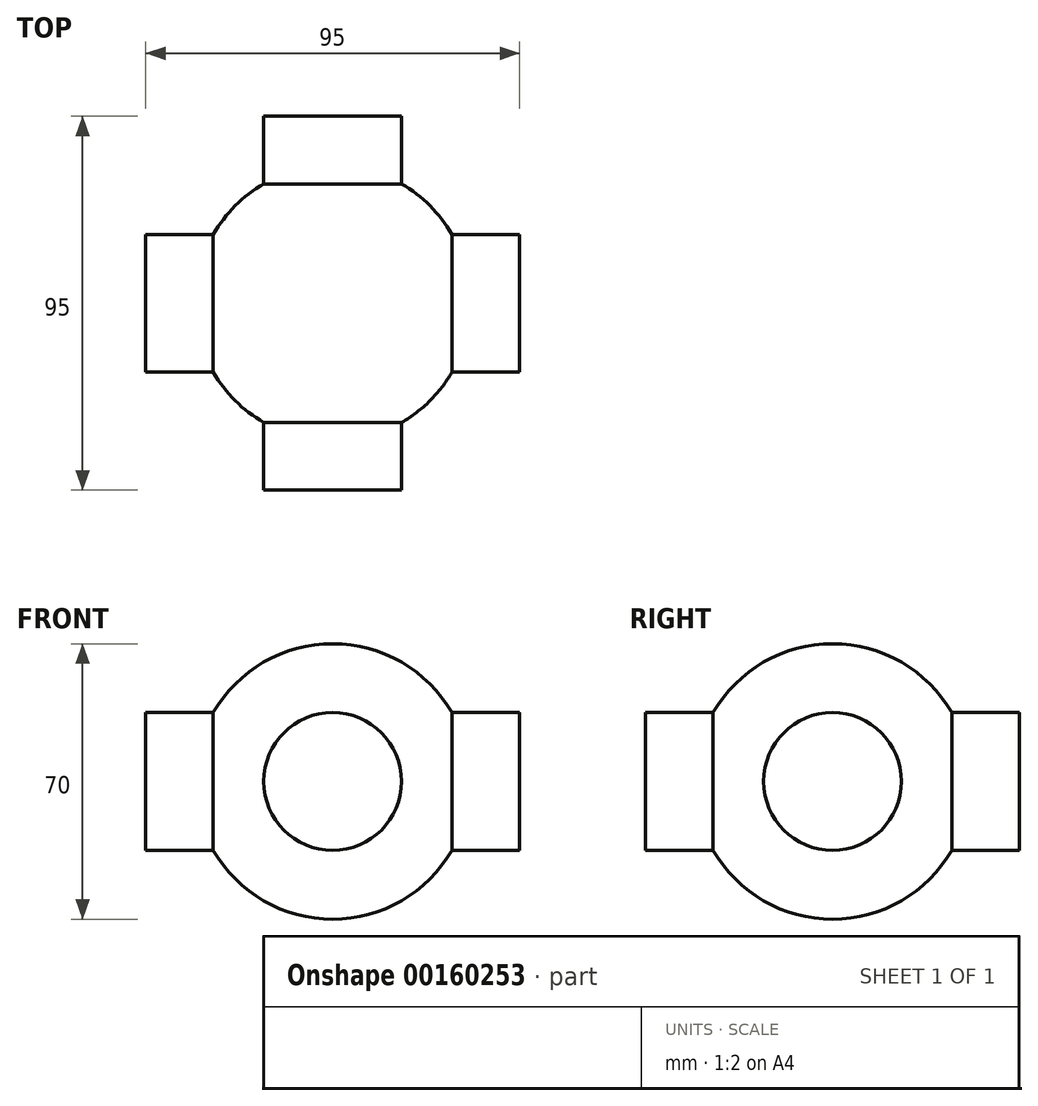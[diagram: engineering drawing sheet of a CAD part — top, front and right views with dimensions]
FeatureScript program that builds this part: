
annotation { "Feature Type Name" : "Feature", "Feature Type Description" : "" }
export const myFeature = defineFeature(function(context is Context, id is Id, definition is map)
    precondition{}
    {
        {
            var Q0;
            Q0=qCreatedBy(makeId("Front.planeOp"),FACE);
            var sketch = newSketch(context, id + "F0", { "sketchPlane" : qUnion([Q0])});
            skArc(sketch, "E0", {"start": v(0, 35) * mm, "mid": v(-35, 0) * mm, "end": v(0, -35) * mm});
            skLineSegment(sketch, "E1", {"start": v(0, 35) * mm, "end": v(0, -35) * mm});
            skSolve(sketch);
        }
        {
            var Q0;
            Q0=qSketchRegion(id+"F0",true);
            var Q1;
            Q1=sQuery(id+"F0.wireOp",EDGE,"E1");
            revolve(context, id + "F1", {"entities" : qUnion([Q0]), "axis" : qUnion([Q1]), "revolveType" : RevolveType.FULL});
        }
        {
            var Q0;
            Q0=qCreatedBy(makeId("Front.planeOp"),FACE);
            var sketch = newSketch(context, id + "F2", { "sketchPlane" : qUnion([Q0])});
            skCircle(sketch, "E2", {"center": v(0, 0) * mm, "radius": 17.5 * mm});
            skSolve(sketch);
        }
        {
            var Q0;
            Q0=qSketchRegion(id+"F2",true);
            extrude(context, id + "F3", {"entities" : qUnion([Q0]), "operationType" : NewBodyOperationType.ADD, "depth" : 95 * mm, "symmetric" : true});
        }
        {
            var Q0;
            Q0=qCreatedBy(makeId("Right.planeOp"),FACE);
            var sketch = newSketch(context, id + "F4", { "sketchPlane" : qUnion([Q0])});
            skCircle(sketch, "E3", {"center": v(0, 0) * mm, "radius": 17.5 * mm});
            skSolve(sketch);
        }
        {
            var Q0;
            Q0=qSketchRegion(id+"F4",true);
            extrude(context, id + "F5", {"entities" : qUnion([Q0]), "operationType" : NewBodyOperationType.ADD, "depth" : 95 * mm, "symmetric" : true});
        }
    });
